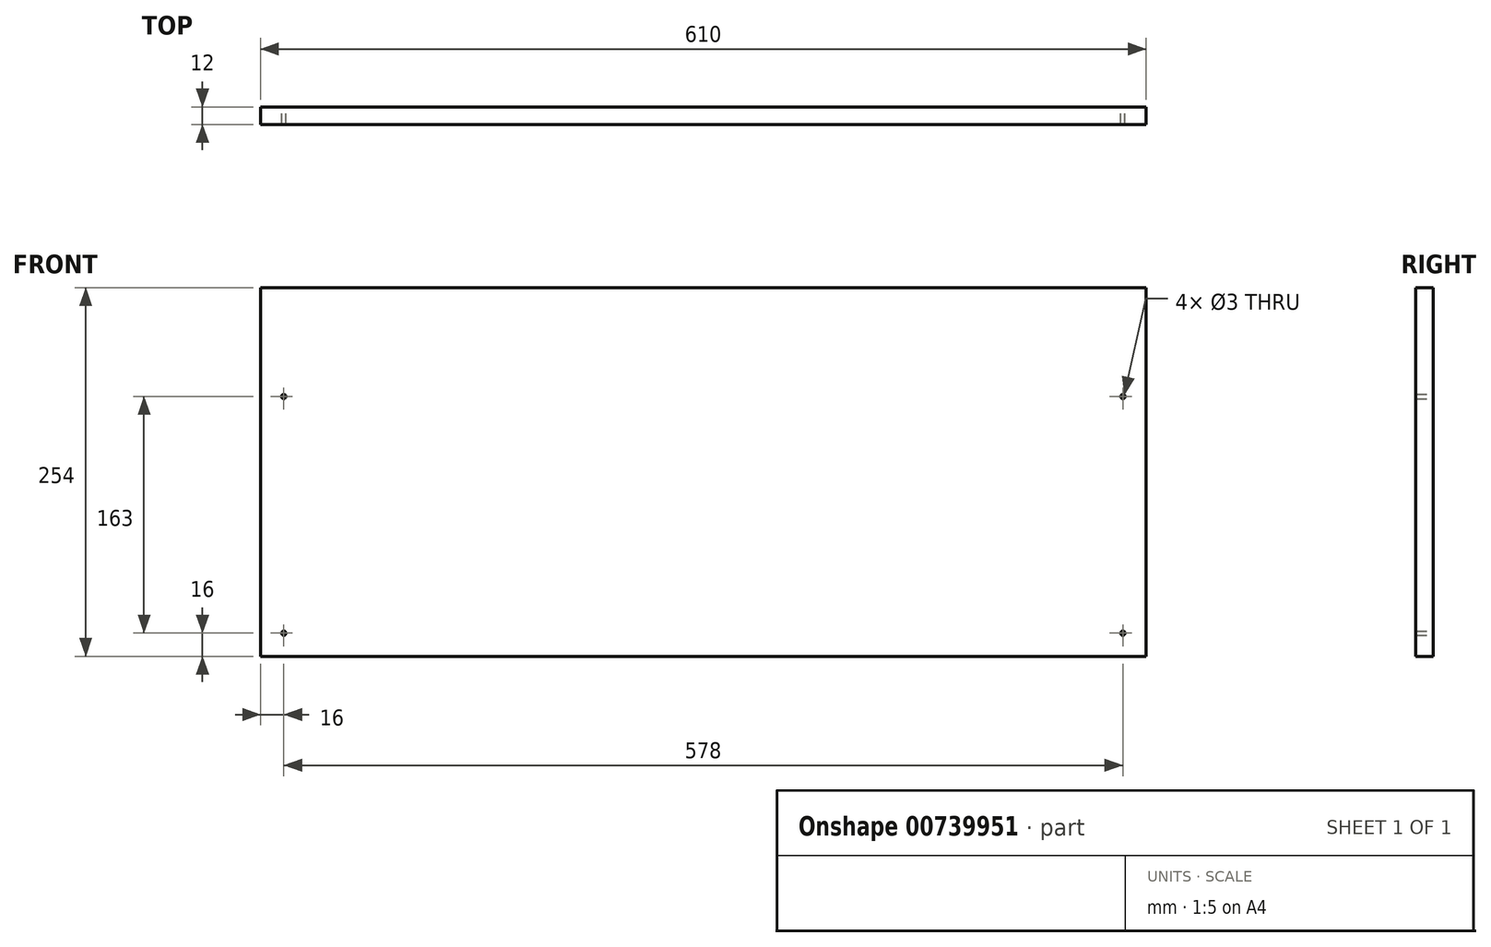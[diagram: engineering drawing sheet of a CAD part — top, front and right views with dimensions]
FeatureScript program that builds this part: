
annotation { "Feature Type Name" : "Feature", "Feature Type Description" : "" }
export const myFeature = defineFeature(function(context is Context, id is Id, definition is map)
    precondition{}
    {
        {
            var Q0;
            Q0=qCreatedBy(makeId("Front.planeOp"),FACE);
            var sketch = newSketch(context, id + "F0", { "sketchPlane" : qUnion([Q0])});
            skLineSegment(sketch, "E0.bottom", {"start": v(305, -127) * mm, "end": v(-305, -127) * mm});
            skLineSegment(sketch, "E0.top", {"start": v(305, 127) * mm, "end": v(-305, 127) * mm});
            skLineSegment(sketch, "E0.left", {"start": v(305, -127) * mm, "end": v(305, 127) * mm});
            skLineSegment(sketch, "E0.right", {"start": v(-305, -127) * mm, "end": v(-305, 127) * mm});
            skPoint(sketch, "E0.middle", {"position": v(0, 0) * mm});
            skLineSegment(sketch, "E1", {"start": v(-289, 127) * mm, "end": v(-289, -127) * mm, "construction": true});
            skCircle(sketch, "E2", {"center": v(-289, 52) * mm, "radius": 1.5 * mm});
            skCircle(sketch, "E3", {"center": v(-289, -111) * mm, "radius": 1.5 * mm});
            skCircle(sketch, "E4.MirrorC", {"center": v(289, -111) * mm, "radius": 1.5 * mm});
            skCircle(sketch, "E5.MirrorC", {"center": v(289, 52) * mm, "radius": 1.5 * mm});
            skLineSegment(sketch, "E6.MirrorCS", {"start": v(289, 127) * mm, "end": v(289, -127) * mm, "construction": true});
            skSolve(sketch);
        }
        {
            var Q0;
            Q0=makeQuery(id+"F0.imprint","IMPRINT",FACE,{"disambiguationData":[TD([[makeQuery(id+"F0.imprint","IMPRINT",EDGE,{"derivedFrom":sQuery(id+"F0.wireOp",EDGE,"E0.bottom")}),-1.0]])]});
            extrude(context, id + "F1", {"entities" : qUnion([Q0]), "depth" : 12 * mm, "offsetDistance" : 25 * mm, "symmetric" : true});
        }
    });
